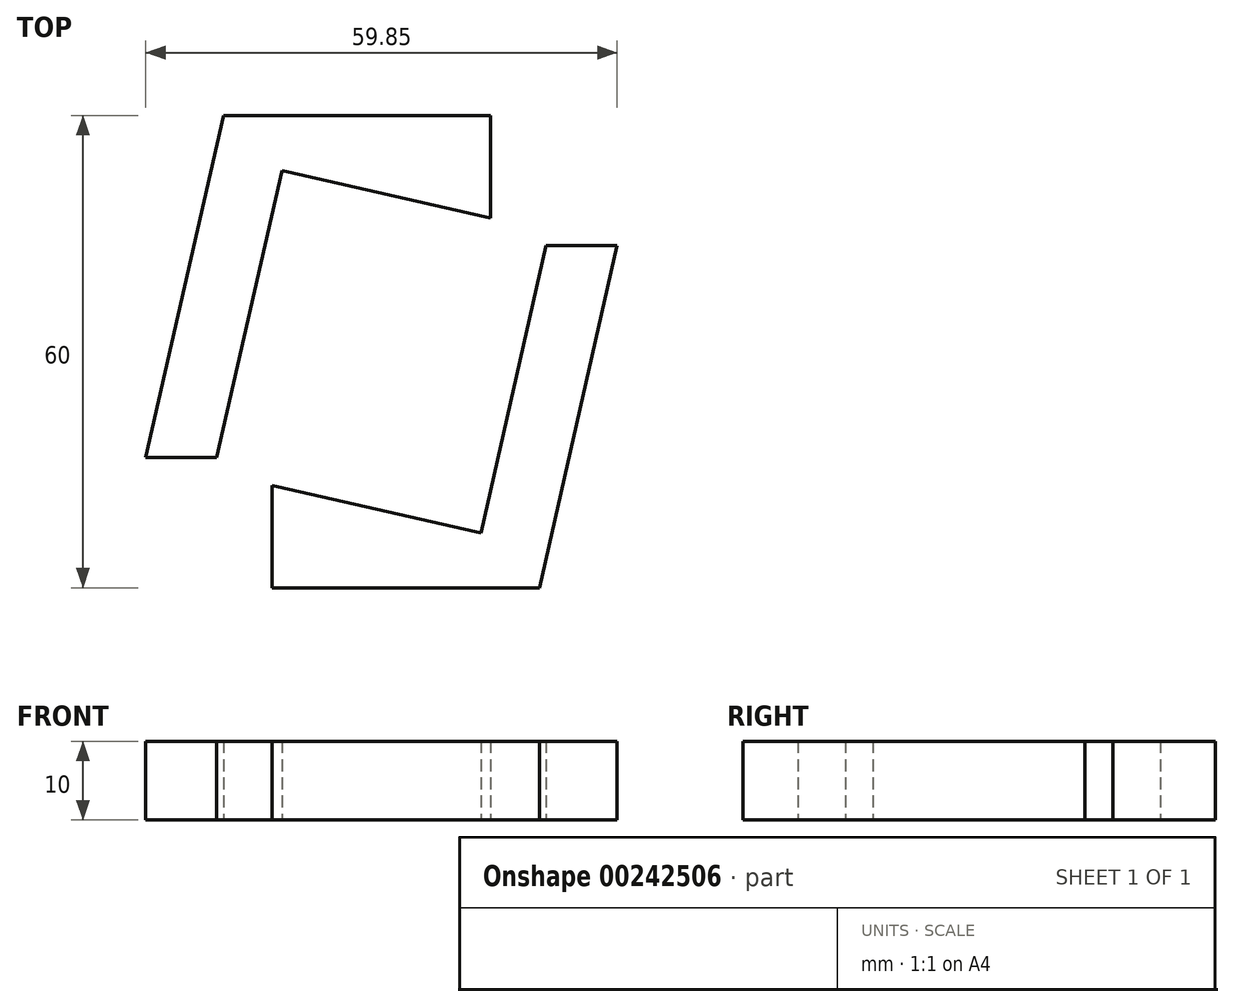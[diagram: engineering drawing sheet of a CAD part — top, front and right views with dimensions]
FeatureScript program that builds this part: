
annotation { "Feature Type Name" : "Feature", "Feature Type Description" : "" }
export const myFeature = defineFeature(function(context is Context, id is Id, definition is map)
    precondition{}
    {
        {
            var Q0;
            Q0=qCreatedBy(makeId("Top.planeOp"),FACE);
            var sketch = newSketch(context, id + "F0", { "sketchPlane" : qUnion([Q0])});
            skLineSegment(sketch, "E0.top", {"start": v(-30, 30) * mm, "end": v(30, 30) * mm, "construction": true});
            skLineSegment(sketch, "E0.left", {"start": v(-30, -30) * mm, "end": v(-30, 30) * mm, "construction": true});
            skLineSegment(sketch, "E0.right", {"start": v(30, -30) * mm, "end": v(30, 30) * mm, "construction": true});
            skPoint(sketch, "E0.middle", {"position": v(0, 0) * mm});
            skLineSegment(sketch, "E1", {"start": v(30, 13.46) * mm, "end": v(21, 13.46) * mm});
            skLineSegment(sketch, "E2", {"start": v(21, 13.46) * mm, "end": v(12.71, -23.03) * mm});
            skLineSegment(sketch, "E3", {"start": v(12.71, -23.03) * mm, "end": v(-13.81, -17) * mm});
            skLineSegment(sketch, "E4", {"start": v(-13.81, -17) * mm, "end": v(-13.81, -30) * mm});
            skLineSegment(sketch, "E5", {"start": v(-13.81, -30) * mm, "end": v(20.13, -30) * mm});
            skLineSegment(sketch, "E6", {"start": v(20.13, -30) * mm, "end": v(30, 13.46) * mm});
            skLineSegment(sketch, "E7", {"start": v(30, 30) * mm, "end": v(-30, -30) * mm, "construction": true});
            skLineSegment(sketch, "E8", {"start": v(-29.85, -13.46) * mm, "end": v(-20.85, -13.46) * mm});
            skLineSegment(sketch, "E9", {"start": v(-20.85, -13.46) * mm, "end": v(-12.56, 23.03) * mm});
            skLineSegment(sketch, "E10", {"start": v(-12.56, 23.03) * mm, "end": v(13.96, 17) * mm});
            skLineSegment(sketch, "E11", {"start": v(13.96, 17) * mm, "end": v(13.96, 30) * mm});
            skLineSegment(sketch, "E12", {"start": v(13.96, 30) * mm, "end": v(-19.98, 30) * mm});
            skLineSegment(sketch, "E13", {"start": v(-19.98, 30) * mm, "end": v(-29.85, -13.46) * mm});
            skSolve(sketch);
        }
        {
            var Q0;
            Q0=makeQuery(id+"F0.imprint","IMPRINT",FACE,{"disambiguationData":[TD([[makeQuery(id+"F0.imprint","IMPRINT",EDGE,{"derivedFrom":sQuery(id+"F0.wireOp",EDGE,"E8")}),1.0]])]});
            var Q1;
            Q1=makeQuery(id+"F0.imprint","IMPRINT",FACE,{"disambiguationData":[TD([[makeQuery(id+"F0.imprint","IMPRINT",EDGE,{"derivedFrom":sQuery(id+"F0.wireOp",EDGE,"E1")}),1.0]])]});
            extrude(context, id + "F1", {"entities" : qUnion([Q0, Q1]), "depth" : 10 * mm});
        }
    });
